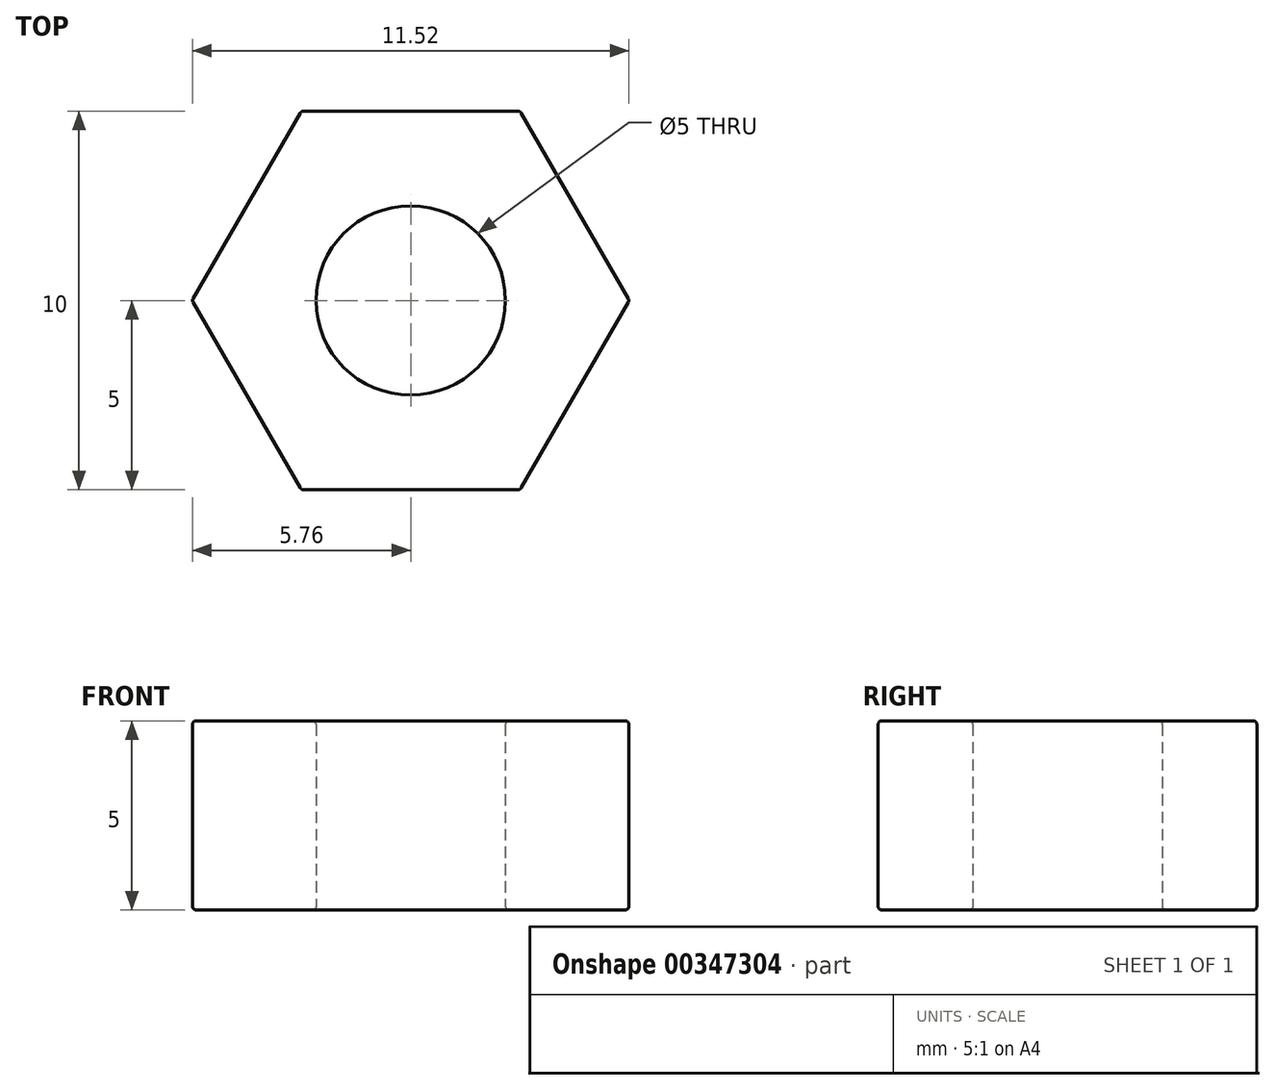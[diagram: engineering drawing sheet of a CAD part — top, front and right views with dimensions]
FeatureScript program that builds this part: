
annotation { "Feature Type Name" : "Feature", "Feature Type Description" : "" }
export const myFeature = defineFeature(function(context is Context, id is Id, definition is map)
    precondition{}
    {
        {
            var Q0;
            Q0=qCreatedBy(makeId("Top.planeOp"),FACE);
            var sketch = newSketch(context, id + "F0", { "sketchPlane" : qUnion([Q0])});
            skCircle(sketch, "E0.cCircle", {"center": v(0, 0) * mm, "radius": 5 * mm, "construction": true});
            skLineSegment(sketch, "E0.0", {"start": v(-2.89, 5) * mm, "end": v(2.89, 5) * mm});
            skLineSegment(sketch, "E0.1", {"start": v(2.89, 5) * mm, "end": v(5.77, 0) * mm});
            skLineSegment(sketch, "E0.2", {"start": v(5.77, 0) * mm, "end": v(2.89, -5) * mm});
            skLineSegment(sketch, "E0.3", {"start": v(2.89, -5) * mm, "end": v(-2.89, -5) * mm});
            skLineSegment(sketch, "E0.4", {"start": v(-2.89, -5) * mm, "end": v(-5.77, 0) * mm});
            skLineSegment(sketch, "E0.5", {"start": v(-5.77, 0) * mm, "end": v(-2.89, 5) * mm});
            skPoint(sketch, "E0.0.midPoint", {"position": v(0, 5) * mm});
            skCircle(sketch, "E1", {"center": v(0, 0) * mm, "radius": 2.5 * mm});
            skSolve(sketch);
        }
        {
            var Q0;
            Q0 = qSketchRegion(id + "F0", true);
            extrude(context, id + "F1", {"entities" : qUnion([Q0]), "depth" : 5 * mm});
        }
        {
            var Q0;
            Q0=makeQuery(id+"F1.opExtrude","CAP_FACE",FACE,{"disambiguationData":[OSD([sQuery(id+"F0.wireOp",EDGE,"E0.0"),sQuery(id+"F0.wireOp",EDGE,"E0.1"),sQuery(id+"F0.wireOp",EDGE,"E0.2"),sQuery(id+"F0.wireOp",EDGE,"E0.3"),sQuery(id+"F0.wireOp",EDGE,"E0.4"),sQuery(id+"F0.wireOp",EDGE,"E0.5"),sQuery(id+"F0.wireOp",EDGE,"E1")])],"isStart":true});
            var Q1;
            Q1=makeQuery(id+"F1.opExtrude","CAP_FACE",FACE,{"disambiguationData":[OSD([sQuery(id+"F0.wireOp",EDGE,"E0.0"),sQuery(id+"F0.wireOp",EDGE,"E0.1"),sQuery(id+"F0.wireOp",EDGE,"E0.2"),sQuery(id+"F0.wireOp",EDGE,"E0.3"),sQuery(id+"F0.wireOp",EDGE,"E0.4"),sQuery(id+"F0.wireOp",EDGE,"E0.5"),sQuery(id+"F0.wireOp",EDGE,"E1")])],"isStart":false});
            fillet(context, id + "F2", {"entities" : qUnion([Q0, Q1]), "radius" : 0.1 * mm, "tangentPropagation" : true, "allowEdgeOverflow" : false});
        }
        {
            var Q0;
            Q0=makeQuery(id+"F1.opExtrude","SWEPT_FACE",FACE,{"disambiguationData":[OSD([sQuery(id+"F0.wireOp",EDGE,"E0.5")])]});
            var Q1;
            Q1=makeQuery(id+"F1.opExtrude","SWEPT_FACE",FACE,{"disambiguationData":[OSD([sQuery(id+"F0.wireOp",EDGE,"E0.0")])]});
            var Q2;
            Q2=makeQuery(id+"F1.opExtrude","SWEPT_FACE",FACE,{"disambiguationData":[OSD([sQuery(id+"F0.wireOp",EDGE,"E0.1")])]});
            var Q3;
            Q3=makeQuery(id+"F1.opExtrude","SWEPT_FACE",FACE,{"disambiguationData":[OSD([sQuery(id+"F0.wireOp",EDGE,"E0.3")])]});
            var Q4;
            Q4=makeQuery(id+"F1.opExtrude","SWEPT_FACE",FACE,{"disambiguationData":[OSD([sQuery(id+"F0.wireOp",EDGE,"E0.2")])]});
            var Q5;
            Q5=makeQuery(id+"F1.opExtrude","SWEPT_FACE",FACE,{"disambiguationData":[OSD([sQuery(id+"F0.wireOp",EDGE,"E0.4")])]});
            fillet(context, id + "F3", {"entities" : qUnion([Q0, Q1, Q2, Q3, Q4, Q5]), "radius" : 0.1 * mm, "tangentPropagation" : true, "allowEdgeOverflow" : false});
        }
    });
